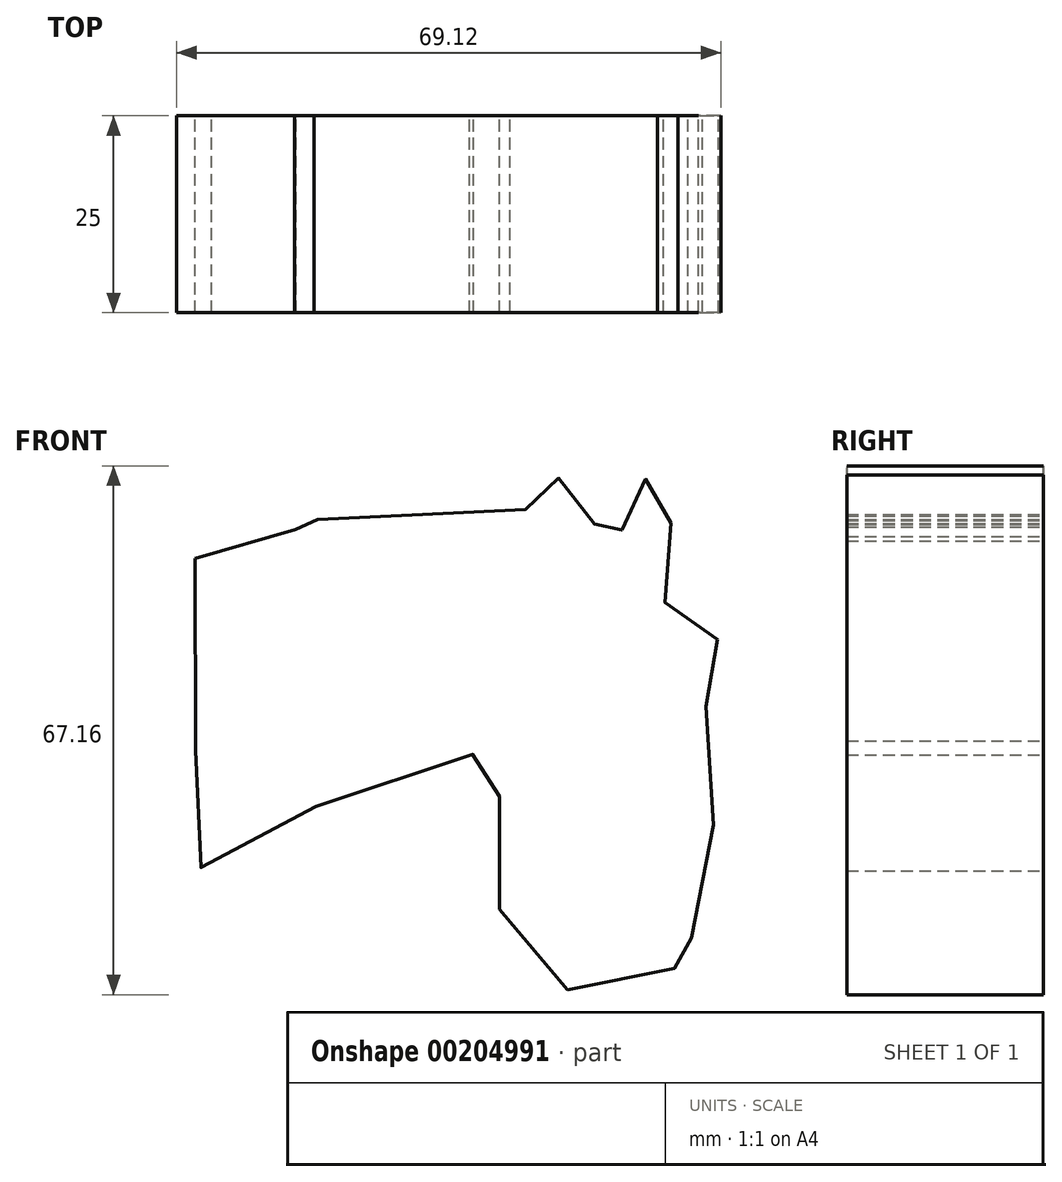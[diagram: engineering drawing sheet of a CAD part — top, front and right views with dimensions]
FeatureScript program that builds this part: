
annotation { "Feature Type Name" : "Feature", "Feature Type Description" : "" }
export const myFeature = defineFeature(function(context is Context, id is Id, definition is map)
    precondition{}
    {
        {
            var Q0;
            Q0=qCreatedBy(makeId("Front.planeOp"),FACE);
            var sketch = newSketch(context, id + "F0", { "sketchPlane" : qUnion([Q0])});
            skFitSpline(sketch, "E0", {"points": [v(-62.79, 5.59) * mm, v(-50.07, 8.25) * mm, v(-50.07, 9.95) * mm, v(-47.64, 8.37) * mm, v(-47.64, 10.2) * mm, v(-45.1, 10.43) * mm, v(-34.92, 11.16) * mm, v(-21.35, 11.4) * mm, v(-20.26, 13.46) * mm, v(-17.48, 17.34) * mm, v(-15.9, 11.77) * mm, v(-14.45, 9.59) * mm, v(-11.06, 9.95) * mm, v(-10.57, 8.5) * mm, v(-9, 7.89) * mm, v(-8.39, 9.83) * mm, v(-6.57, 12.37) * mm, v(-5.97, 15.16) * mm, v(-4.27, 16.13) * mm, v(-3.9, 12.25) * mm, v(-1.48, 8.5) * mm, v(-3.3, 0.98) * mm, v(-1.85, -1.08) * mm, v(1.67, -2.53) * mm, v(3.97, -6.9) * mm, v(1.67, -12.1) * mm, v(2.76, -14.16) * mm, v(2.63, -30.4) * mm, v(0, -42.33) * mm, v(1.11, -43.2) * mm, v(0, -45.71) * mm, v(-1.15, -45.96) * mm, v(-5.37, -49) * mm, v(-20.59, -46.94) * mm, v(-24.04, -38.3) * mm, v(-23.07, -27.84) * mm, v(-27.93, -17.58) * mm, v(-27.39, -18.99) * mm, v(-31.92, -19.64) * mm, v(-62.79, -34.1) * mm, v(-61.82, -33.45) * mm, v(-60.95, -27.08) * mm, v(-62.79, 5.59) * mm]});
            skSolve(sketch);
        }
        {
            var Q0;
            Q0 = qSketchRegion(id + "F0", true);
            extrude(context, id + "F1", {"entities" : qUnion([Q0]), "depth" : 25 * mm});
        }
    });
